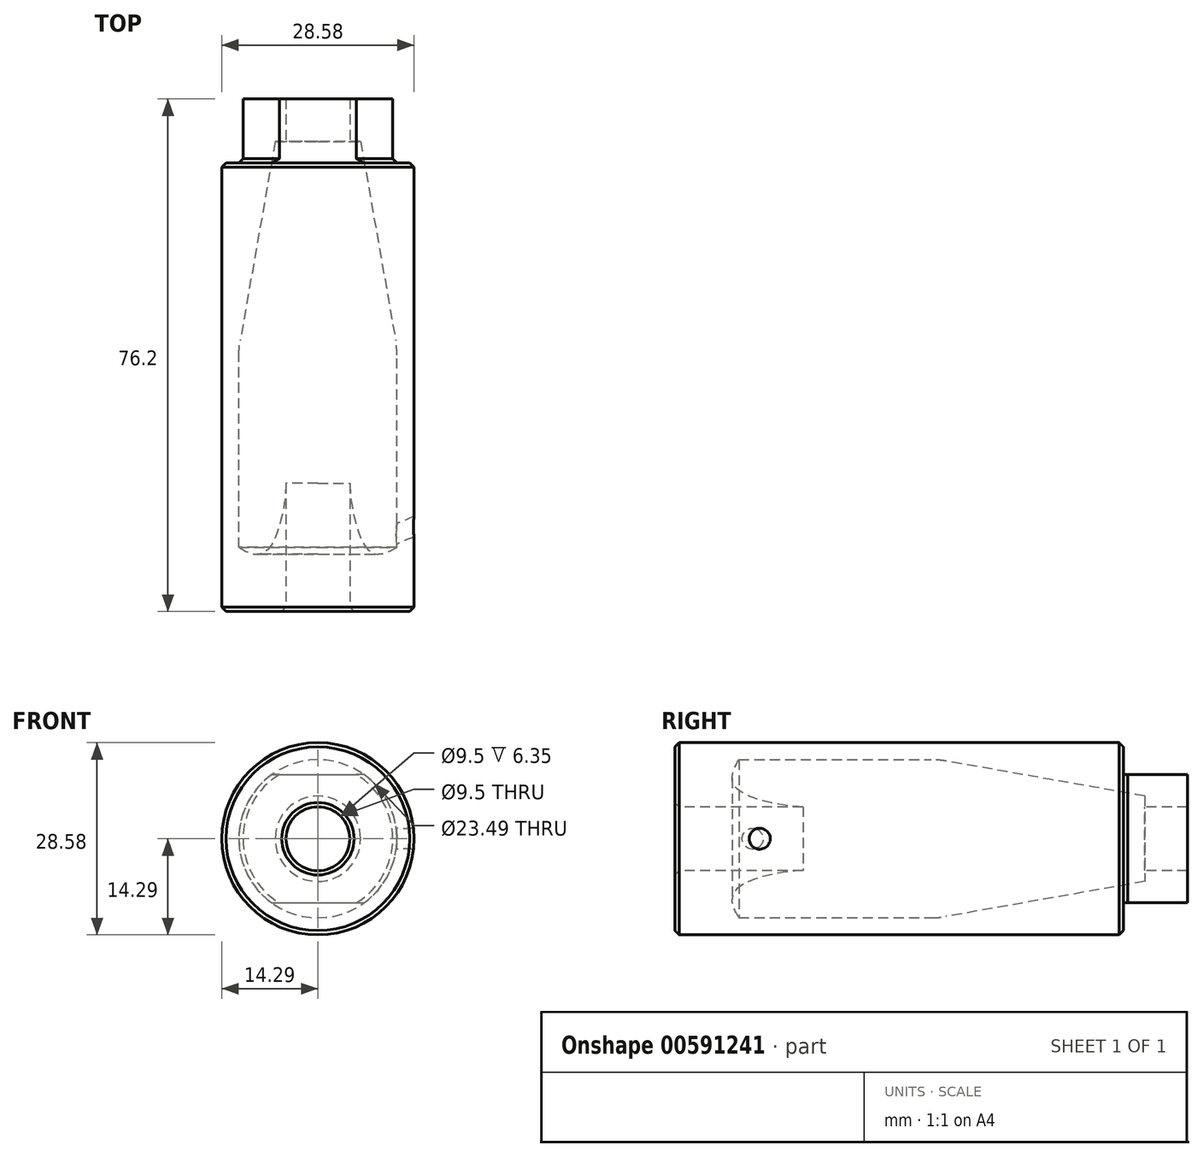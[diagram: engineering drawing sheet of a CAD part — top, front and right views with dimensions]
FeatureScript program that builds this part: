
annotation { "Feature Type Name" : "Feature", "Feature Type Description" : "" }
export const myFeature = defineFeature(function(context is Context, id is Id, definition is map)
    precondition{}
    {
        {
            var Q0;
            Q0=qCreatedBy(makeId("Front.planeOp"),FACE);
            var sketch = newSketch(context, id + "F0", { "sketchPlane" : qUnion([Q0])});
            skCircle(sketch, "E0", {"center": v(0, 0) * mm, "radius": 14.29 * mm});
            skCircle(sketch, "E1", {"center": v(0, 0) * mm, "radius": 4.75 * mm});
            skSolve(sketch);
        }
        {
            var Q0;
            Q0=makeQuery(id+"F0.imprint","IMPRINT",FACE,{"disambiguationData":[TD([[makeQuery(id+"F0.imprint","IMPRINT",EDGE,{"derivedFrom":sQuery(id+"F0.wireOp",EDGE,"E0")}),1.0]])]});
            extrude(context, id + "F1", {"entities" : qUnion([Q0]), "oppositeDirection" : true, "depth" : 76.2 * mm, "offsetDistance" : 25.4 * mm});
        }
        {
            var Q0;
            Q0=qCreatedBy(makeId("Right.planeOp"),FACE);
            var sketch = newSketch(context, id + "F2", { "sketchPlane" : qUnion([Q0])});
            skLineSegment(sketch, "E2.0", {"start": v(76.2, -14.29) * mm, "end": v(76.2, 14.29) * mm, "construction": true});
            skLineSegment(sketch, "E3", {"start": v(0, 4.75) * mm, "end": v(76.2, 4.75) * mm, "construction": true});
            skLineSegment(sketch, "E4", {"start": v(76.2, -4.75) * mm, "end": v(0, -4.75) * mm, "construction": true});
            skLineSegment(sketch, "E5", {"start": v(0, 14.29) * mm, "end": v(76.2, 14.29) * mm, "construction": true});
            skLineSegment(sketch, "E6", {"start": v(76.2, -14.29) * mm, "end": v(0, -14.29) * mm, "construction": true});
            skLineSegment(sketch, "E7.0.0", {"start": v(0, -14.29) * mm, "end": v(0, 14.29) * mm, "construction": true});
            skLineSegment(sketch, "E8", {"start": v(9.53, 11.75) * mm, "end": v(38.1, 11.75) * mm});
            skLineSegment(sketch, "E9", {"start": v(40.3, 11.55) * mm, "end": v(69.85, 6.35) * mm});
            skPoint(sketch, "E10.visualSharp", {"position": v(39.21, 11.75) * mm});
            skArc(sketch, "E10.filletArc", {"start": v(40.3, 11.55) * mm, "mid": v(39.2, 11.7) * mm, "end": v(38.1, 11.75) * mm});
            skLineSegment(sketch, "E11", {"start": v(0, 0) * mm, "end": v(76.2, 0) * mm, "construction": true});
            skLineSegment(sketch, "E12", {"start": v(69.85, 6.35) * mm, "end": v(69.85, 4.75) * mm});
            skLineSegment(sketch, "E13", {"start": v(69.85, 4.75) * mm, "end": v(19.05, 4.75) * mm});
            skFitSpline(sketch, "E14", {"points": [v(19.05, 4.75) * mm, v(8.82, 7.92) * mm, v(9.53, 11.75) * mm], "startDerivative": vector(-14.15, 0) * mm, "endDerivative": vector(4.8, 8.21) * mm});
            skSolve(sketch);
        }
        {
            var Q0;
            Q0 = qSketchRegion(id + "F2", true);
            var Q1;
            Q1=sQuery(id+"F2.wireOp",EDGE,"E11");
            revolve(context, id + "F3", {"operationType" : NewBodyOperationType.REMOVE, "entities" : qUnion([Q0]), "axis" : qUnion([Q1]), "revolveType" : RevolveType.FULL, "oppositeDirection" : true});
        }
        {
            var Q0;
            Q0=qCreatedBy(makeId("Right.planeOp"),FACE);
            cPlane(context, id + "F4", {"entities" : qUnion([Q0]), "cplaneType" : CPlaneType.OFFSET, "offset" : 11.43 * mm, "width" : 152.4 * mm, "height" : 152.4 * mm});
        }
        {
            var Q0;
            Q0=qCreatedBy(id+"F4.planeOp",FACE);
            var sketch = newSketch(context, id + "F5", { "sketchPlane" : qUnion([Q0])});
            skCircle(sketch, "E15", {"center": v(11.43, 0) * mm, "radius": 1.59 * mm});
            skSolve(sketch);
        }
        {
            var Q0;
            Q0=qCreatedBy(makeId("Right.planeOp"),FACE);
            cPlane(context, id + "F6", {"entities" : qUnion([Q0]), "cplaneType" : CPlaneType.OFFSET, "offset" : 14.48 * mm, "width" : 152.4 * mm, "height" : 152.4 * mm});
        }
        {
            var Q0;
            Q0=qCreatedBy(id+"F6.planeOp",FACE);
            var sketch = newSketch(context, id + "F7", { "sketchPlane" : qUnion([Q0])});
            skCircle(sketch, "E16", {"center": v(12.7, 0) * mm, "radius": 1.59 * mm});
            skSolve(sketch);
        }
        {
            var Q1;
            Q1 = qSketchRegion(id + "F7", true);
            var Q2;
            Q2 = qSketchRegion(id + "F5", true);
            loft(context, id + "F8", {"operationType" : NewBodyOperationType.REMOVE, "sheetProfilesArray" : [{ "sheetProfileEntities" : qUnion([Q1]) }, { "sheetProfileEntities" : qUnion([Q2]) }]});
        }
        {
            var Q0;
            Q0=qCreatedBy(makeId("Top.planeOp"),FACE);
            var sketch = newSketch(context, id + "F9", { "sketchPlane" : qUnion([Q0])});
            skLineSegment(sketch, "E17", {"start": v(0, 0) * mm, "end": v(0, 77.4) * mm, "construction": true});
            skSolve(sketch);
        }
        {
            var Q0;
            Q0=qCreatedBy(makeId("Right.planeOp"),FACE);
            var sketch = newSketch(context, id + "F10", { "sketchPlane" : qUnion([Q0])});
            skLineSegment(sketch, "E18.bottom", {"start": v(66.67, 22.82) * mm, "end": v(76.2, 22.82) * mm});
            skLineSegment(sketch, "E18.top", {"start": v(66.67, 11.11) * mm, "end": v(76.2, 11.11) * mm});
            skLineSegment(sketch, "E18.left", {"start": v(66.67, 22.82) * mm, "end": v(66.67, 11.11) * mm});
            skLineSegment(sketch, "E18.right", {"start": v(76.2, 22.82) * mm, "end": v(76.2, 11.11) * mm});
            skLineSegment(sketch, "E19", {"start": v(76.3, 0) * mm, "end": v(64.17, 0) * mm, "construction": true});
            skSolve(sketch);
        }
        {
            var Q0;
            Q0=makeQuery(id+"F10.imprint","IMPRINT",FACE,{"disambiguationData":[TD([[makeQuery(id+"F10.imprint","IMPRINT",EDGE,{"derivedFrom":sQuery(id+"F10.wireOp",EDGE,"E18.bottom")}),-1.0]])]});
            var Q1;
            Q1=sQuery(id+"F10.wireOp",EDGE,"E19");
            var Q2;
            Q2=sQuery(id+"F10.wireOp",EDGE,"E19");
            revolve(context, id + "F11", {"operationType" : NewBodyOperationType.REMOVE, "entities" : qUnion([Q0]), "surfaceEntities" : qUnion([Q1]), "axis" : qUnion([Q2]), "revolveType" : RevolveType.FULL, "oppositeDirection" : true});
        }
        {
            var Q0;
            Q0=qCreatedBy(makeId("Right.planeOp"),FACE);
            var sketch = newSketch(context, id + "F12", { "sketchPlane" : qUnion([Q0])});
            skLineSegment(sketch, "E20", {"start": v(0, 14.29) * mm, "end": v(66.67, 14.29) * mm, "construction": true});
            skLineSegment(sketch, "E21", {"start": v(66.67, -14.29) * mm, "end": v(0, -14.29) * mm, "construction": true});
            skLineSegment(sketch, "E22.bottom", {"start": v(66.67, 9.53) * mm, "end": v(76.2, 9.53) * mm});
            skLineSegment(sketch, "E22.top", {"start": v(66.67, 17.14) * mm, "end": v(76.2, 17.14) * mm});
            skLineSegment(sketch, "E22.left", {"start": v(66.67, 9.53) * mm, "end": v(66.67, 17.14) * mm});
            skLineSegment(sketch, "E22.right", {"start": v(76.2, 9.53) * mm, "end": v(76.2, 17.14) * mm});
            skLineSegment(sketch, "E23.MirrorCS", {"start": v(66.67, -17.14) * mm, "end": v(76.2, -17.14) * mm});
            skLineSegment(sketch, "E24.MirrorCS", {"start": v(66.67, -9.53) * mm, "end": v(76.2, -9.53) * mm});
            skLineSegment(sketch, "E25.MirrorCS", {"start": v(76.2, -9.53) * mm, "end": v(76.2, -17.14) * mm});
            skLineSegment(sketch, "E26.MirrorCS", {"start": v(66.67, -9.53) * mm, "end": v(66.67, -17.14) * mm});
            skSolve(sketch);
        }
        {
            var Q0;
            Q0 = qSketchRegion(id + "F12", true);
            extrude(context, id + "F13", {"entities" : qUnion([Q0]), "operationType" : NewBodyOperationType.REMOVE, "endBound" : BoundingType.SYMMETRIC, "oppositeDirection" : true, "depth" : 25.4 * mm, "offsetDistance" : 25.4 * mm});
        }
        {
            var Q0;
            Q0=makeQuery(id+"F1.opExtrude","CAP_EDGE",EDGE,{"disambiguationData":[OSD([sQuery(id+"F0.wireOp",EDGE,"E0")])],"isStart":true});
            chamfer(context, id + "F14", {"entities" : qUnion([Q0]), "width" : 0.64 * mm, "tangentPropagation" : true});
        }
        {
            var Q0;
            Q0=makeQuery(id+"F13.boolean.opBoolean","INTERSECT",EDGE,{"derivedFrom":[makeQuery(id+"F13.opExtrude","SWEPT_FACE",FACE,{"disambiguationData":[OSD([sQuery(id+"F12.wireOp",EDGE,"E22.left")])]}),makeQuery(id+"F13.opExtrude","SWEPT_FACE",FACE,{"disambiguationData":[OSD([sQuery(id+"F12.wireOp",EDGE,"E26.MirrorCS")])]})]});
            chamfer(context, id + "F15", {"entities" : qUnion([Q0]), "width" : 0.64 * mm, "tangentPropagation" : true});
        }
        {
            var Q0;
            Q0=makeQuery(id+"F13.boolean.opBoolean","SPLIT",EDGE,{"disambiguationData":[OD(0.0)],"derivedFrom":makeQuery(id+"F11.boolean.opBoolean","COPY",EDGE,{"derivedFrom":makeQuery(id+"F11.opRevolve","SWEPT_EDGE",EDGE,{"disambiguationData":[OSD([sQuery(id+"F10.wireOp",EDGE,"E18.top"),sQuery(id+"F10.wireOp",EDGE,"E18.right")])]})})});
            var Q1;
            Q1=makeQuery(id+"F13.boolean.opBoolean","SPLIT",EDGE,{"disambiguationData":[OD(1.0)],"derivedFrom":makeQuery(id+"F11.boolean.opBoolean","COPY",EDGE,{"derivedFrom":makeQuery(id+"F11.opRevolve","SWEPT_EDGE",EDGE,{"disambiguationData":[OSD([sQuery(id+"F10.wireOp",EDGE,"E18.top"),sQuery(id+"F10.wireOp",EDGE,"E18.right")])]})})});
            var Q2;
            Q2=makeQuery(id+"F13.boolean.opBoolean","SPLIT",EDGE,{"disambiguationData":[OD(1.0)],"derivedFrom":makeQuery(id+"F11.boolean.opBoolean","COPY",EDGE,{"derivedFrom":makeQuery(id+"F11.opRevolve","SWEPT_EDGE",EDGE,{"disambiguationData":[OSD([sQuery(id+"F10.wireOp",EDGE,"E18.top"),sQuery(id+"F10.wireOp",EDGE,"E18.left")])]})})});
            var Q3;
            Q3=makeQuery(id+"F13.boolean.opBoolean","SPLIT",EDGE,{"disambiguationData":[OD(0.0)],"derivedFrom":makeQuery(id+"F11.boolean.opBoolean","COPY",EDGE,{"derivedFrom":makeQuery(id+"F11.opRevolve","SWEPT_EDGE",EDGE,{"disambiguationData":[OSD([sQuery(id+"F10.wireOp",EDGE,"E18.top"),sQuery(id+"F10.wireOp",EDGE,"E18.left")])]})})});
            chamfer(context, id + "F16", {"entities" : qUnion([Q0, Q1, Q2, Q3]), "width" : 0.64 * mm, "tangentPropagation" : true});
        }
        {
            var Q0;
            Q0=makeQuery(id+"F1.opExtrude","CAP_EDGE",EDGE,{"disambiguationData":[OSD([sQuery(id+"F0.wireOp",EDGE,"E1")])],"isStart":true});
            chamfer(context, id + "F17", {"entities" : qUnion([Q0]), "width" : 0.64 * mm, "tangentPropagation" : true});
        }
    });
